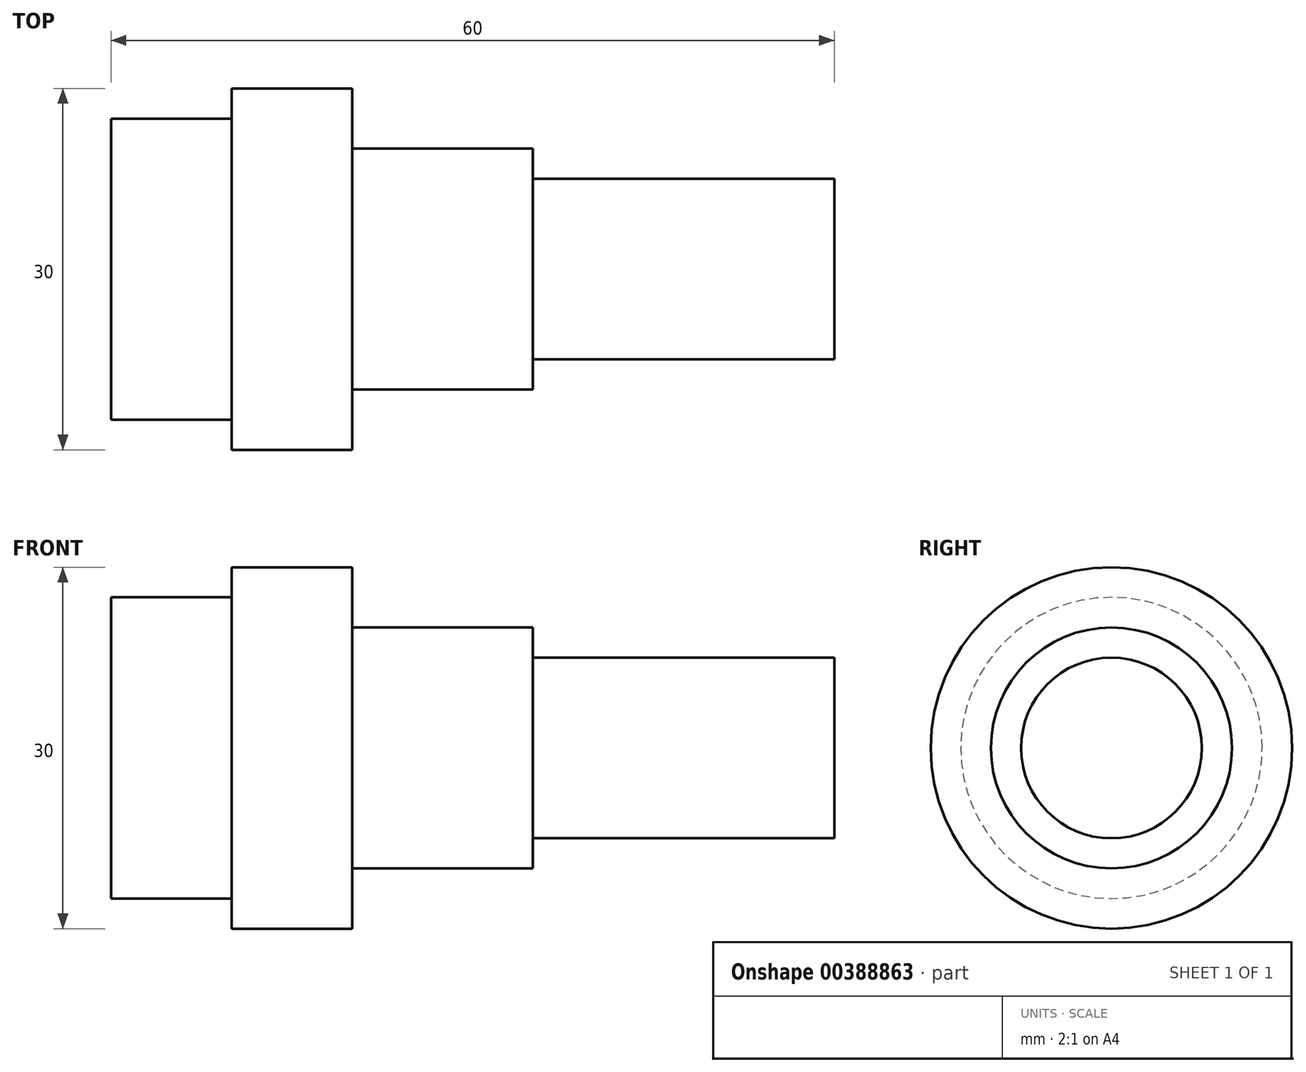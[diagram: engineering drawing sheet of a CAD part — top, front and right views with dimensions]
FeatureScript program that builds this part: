
annotation { "Feature Type Name" : "Feature", "Feature Type Description" : "" }
export const myFeature = defineFeature(function(context is Context, id is Id, definition is map)
    precondition{}
    {
        {
            var Q0;
            Q0=qCreatedBy(makeId("Right.planeOp"),FACE);
            var sketch = newSketch(context, id + "F0", { "sketchPlane" : qUnion([Q0])});
            skCircle(sketch, "E0", {"center": v(0, 0) * mm, "radius": 7.5 * mm});
            skSolve(sketch);
        }
        {
            var Q0;
            Q0 = qSketchRegion(id + "F0", true);
            extrude(context, id + "F1", {"entities" : qUnion([Q0]), "depth" : 25 * mm});
        }
        {
            var Q0;
            Q0=makeQuery(id+"F1.opExtrude","CAP_FACE",FACE,{"disambiguationData":[OSD([sQuery(id+"F0.wireOp",EDGE,"E0")])],"isStart":true});
            var sketch = newSketch(context, id + "F2", { "sketchPlane" : qUnion([Q0])});
            skCircle(sketch, "E1", {"center": v(0, 0) * mm, "radius": 10 * mm});
            skSolve(sketch);
        }
        {
            var Q0;
            Q0 = qSketchRegion(id + "F2", true);
            extrude(context, id + "F3", {"entities" : qUnion([Q0]), "operationType" : NewBodyOperationType.ADD, "depth" : 15 * mm});
        }
        {
            var Q0;
            Q0=makeQuery(id+"F3.opExtrude","CAP_FACE",FACE,{"disambiguationData":[OSD([sQuery(id+"F2.wireOp",EDGE,"E1")])],"isStart":false});
            var sketch = newSketch(context, id + "F4", { "sketchPlane" : qUnion([Q0])});
            skCircle(sketch, "E2", {"center": v(0, 0) * mm, "radius": 15 * mm});
            skSolve(sketch);
        }
        {
            var Q0;
            Q0 = qSketchRegion(id + "F4", true);
            extrude(context, id + "F5", {"entities" : qUnion([Q0]), "operationType" : NewBodyOperationType.ADD, "depth" : 10 * mm});
        }
        {
            var Q0;
            Q0=makeQuery(id+"F5.opExtrude","CAP_FACE",FACE,{"disambiguationData":[OSD([sQuery(id+"F4.wireOp",EDGE,"E2")])],"isStart":false});
            var sketch = newSketch(context, id + "F6", { "sketchPlane" : qUnion([Q0])});
            skCircle(sketch, "E3", {"center": v(0, 0) * mm, "radius": 12.5 * mm});
            skSolve(sketch);
        }
        {
            var Q0;
            Q0=makeQuery(id+"F6.imprint","IMPRINT",FACE,{"disambiguationData":[TD([[makeQuery(id+"F6.imprint","IMPRINT",EDGE,{"derivedFrom":sQuery(id+"F6.wireOp",EDGE,"E3")}),1.0]])]});
            extrude(context, id + "F7", {"entities" : qUnion([Q0]), "operationType" : NewBodyOperationType.ADD, "depth" : 10 * mm});
        }
    });
